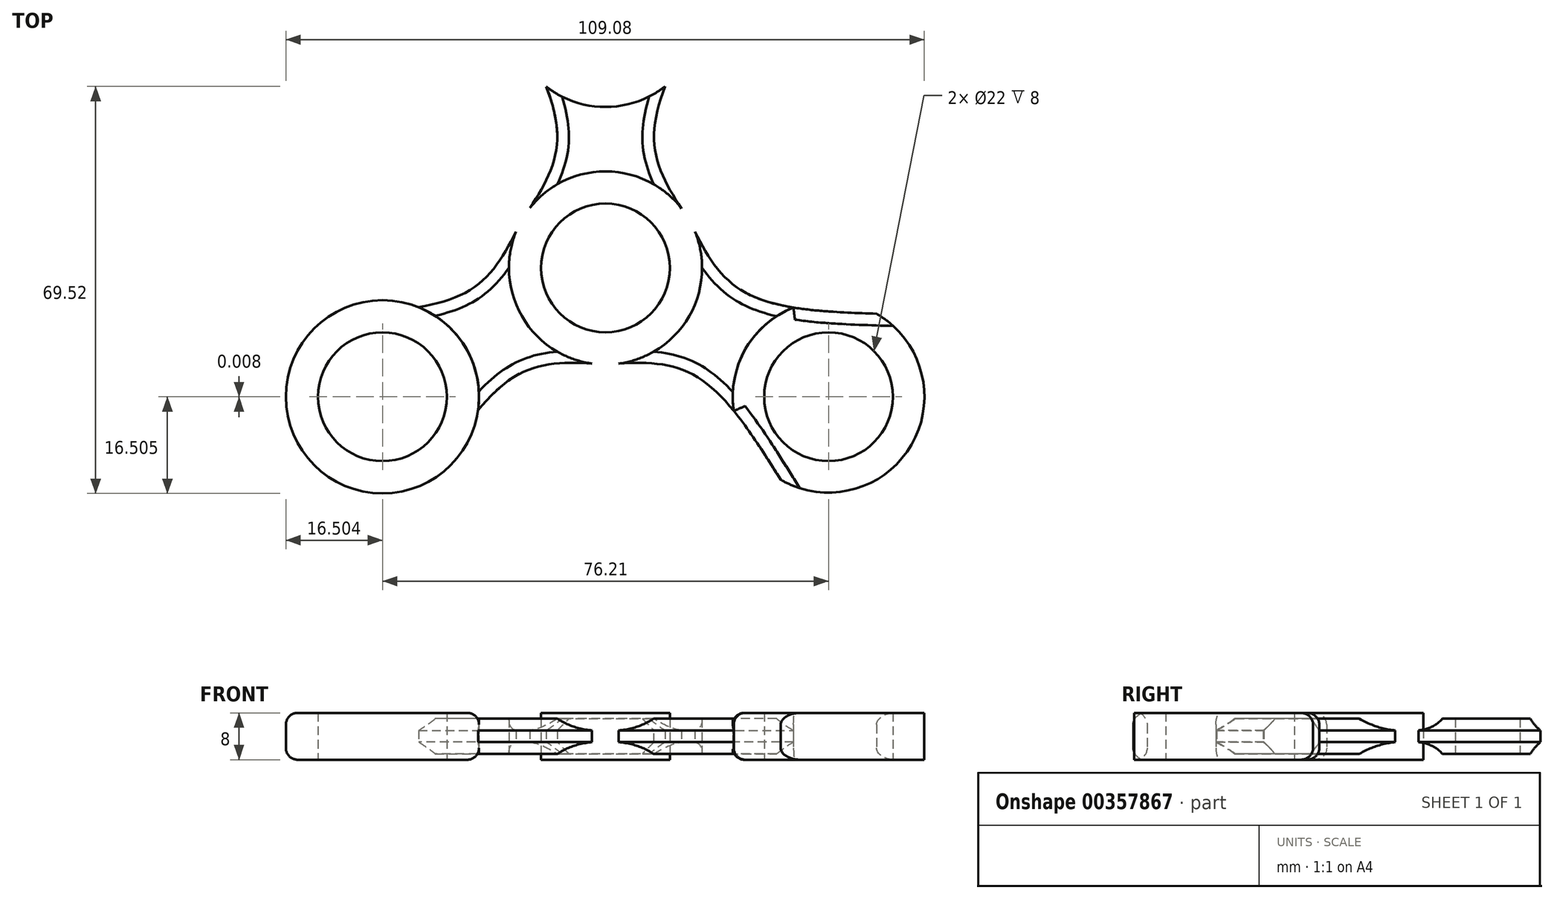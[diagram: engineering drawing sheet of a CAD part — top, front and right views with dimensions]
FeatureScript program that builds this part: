
annotation { "Feature Type Name" : "Feature", "Feature Type Description" : "" }
export const myFeature = defineFeature(function(context is Context, id is Id, definition is map)
    precondition{}
    {
        {
            var Q0;
            Q0=qCreatedBy(makeId("Top.planeOp"),FACE);
            var sketch = newSketch(context, id + "F0", { "sketchPlane" : qUnion([Q0])});
            skCircle(sketch, "E0", {"center": v(0.06, -10.15) * mm, "radius": 11 * mm});
            skCircle(sketch, "E1", {"center": v(0.06, 33.85) * mm, "radius": 11 * mm});
            skCircle(sketch, "E2", {"center": v(38.16, -32.15) * mm, "radius": 11 * mm});
            skCircle(sketch, "E3", {"center": v(-38.05, -32.16) * mm, "radius": 11 * mm});
            skCircle(sketch, "E4.0", {"center": v(0.06, -10.15) * mm, "radius": 16.5 * mm});
            skCircle(sketch, "E5.0", {"center": v(0.06, 33.85) * mm, "radius": 16.5 * mm});
            skCircle(sketch, "E6.0", {"center": v(-38.05, -32.16) * mm, "radius": 16.5 * mm});
            skLineSegment(sketch, "E7", {"start": v(0.06, 11.85) * mm, "end": v(0.06, 11.85) * mm});
            skPoint(sketch, "E8.endSnap0", {"position": v(19.11, -21.15) * mm});
            skLineSegment(sketch, "E9", {"start": v(29.98, -46.32) * mm, "end": v(29.98, -46.32) * mm});
            skLineSegment(sketch, "E10", {"start": v(-10.06, 20.82) * mm, "end": v(-10.06, 20.82) * mm});
            skLineSegment(sketch, "E11", {"start": v(10.23, 20.86) * mm, "end": v(10.23, 20.86) * mm});
            skFitSpline(sketch, "E12", {"points": [v(46.35, -17.97) * mm, v(23.26, -13.96) * mm, v(14.35, -1.9) * mm], "startDerivative": vector(-47.53, 1.69) * mm, "endDerivative": vector(-15.28, 31.57) * mm});
            skLineSegment(sketch, "E13", {"start": v(21.98, -34.58) * mm, "end": v(21.98, -34.58) * mm});
            skArc(sketch, "E14", {"start": v(23.99, -23.96) * mm, "mid": v(22.08, -29.1) * mm, "end": v(21.98, -34.58) * mm});
            skFitSpline(sketch, "E15", {"points": [v(-29.8, -46.44) * mm, v(-14.84, -28.33) * mm, v(0.06, -26.65) * mm], "startDerivative": vector(25.05, 40.57) * mm, "endDerivative": vector(35.03, -2.6) * mm});
            skFitSpline(sketch, "E16", {"points": [v(16.56, 33.85) * mm, v(8.36, 11.85) * mm, v(14.35, -1.9) * mm], "startDerivative": vector(-22.6, -41.98) * mm, "endDerivative": vector(19.75, -29.04) * mm});
            skFitSpline(sketch, "E17", {"points": [v(-16.44, 33.85) * mm, v(-8.2, 11.85) * mm, v(-14.23, -1.9) * mm], "startDerivative": vector(22.75, -41.99) * mm, "endDerivative": vector(-19.91, -29.03) * mm});
            skArc(sketch, "E18", {"start": v(21.98, -34.58) * mm, "mid": v(24.64, -41.37) * mm, "end": v(29.98, -46.32) * mm});
            skArc(sketch, "E19", {"start": v(29.98, -46.32) * mm, "mid": v(53.98, -27.9) * mm, "end": v(23.99, -23.96) * mm});
            skFitSpline(sketch, "E20", {"points": [v(-46.3, -17.87) * mm, v(-23.14, -13.96) * mm, v(-14.23, -1.9) * mm], "startDerivative": vector(47.65, 1.44) * mm, "endDerivative": vector(15.27, 31.62) * mm});
            skFitSpline(sketch, "E21", {"points": [v(0.06, -26.65) * mm, v(14.96, -28.33) * mm, v(29.98, -46.32) * mm], "startDerivative": vector(34.97, 2.55) * mm, "endDerivative": vector(25.23, -40.32) * mm});
            skSolve(sketch);
        }
        {
            var Q0;
            {var subQ0=sQuery(id+"F0.wireOp",EDGE,"E20");var subQ1=sQuery(id+"F0.wireOp",EDGE,"E4.0");var subQ2=makeQuery(id+"F0.imprint","INTERSECT",VERTEX,{"derivedFrom":[subQ1,subQ0]});Q0=makeQuery(id+"F0.imprint","IMPRINT",FACE,{"disambiguationData":[TD([[makeQuery(id+"F0.imprint","IMPRINT",EDGE,{"disambiguationData":[TD([[subQ2,-1.0]])],"derivedFrom":subQ1}),-1.0]])]});}
            var Q1;
            {var subQ0=sQuery(id+"F0.wireOp",EDGE,"E16");var subQ1=sQuery(id+"F0.wireOp",EDGE,"E4.0");var subQ2=makeQuery(id+"F0.imprint","INTERSECT",VERTEX,{"derivedFrom":[subQ1,subQ0]});Q1=makeQuery(id+"F0.imprint","IMPRINT",FACE,{"disambiguationData":[TD([[makeQuery(id+"F0.imprint","IMPRINT",EDGE,{"disambiguationData":[TD([[subQ2,-1.0]])],"derivedFrom":subQ1}),-1.0]])]});}
            var Q2;
            {var subQ3=sQuery(id+"F0.wireOp",EDGE,"E14");Q2=makeQuery(id+"F0.imprint","IMPRINT",FACE,{"disambiguationData":[TD([[makeQuery(id+"F0.imprint","IMPRINT",EDGE,{"derivedFrom":subQ3}),-1.0]])]});}
            extrude(context, id + "F1", {"entities" : qUnion([Q0, Q1, Q2]), "depth" : 6 * mm, "symmetric" : true});
        }
        {
            var Q0;
            Q0=makeQuery(id+"F0.imprint","IMPRINT",FACE,{"disambiguationData":[TD([[makeQuery(id+"F0.imprint","IMPRINT",EDGE,{"derivedFrom":sQuery(id+"F0.wireOp",EDGE,"E1")}),-1.0]])]});
            var Q1;
            Q1=makeQuery(id+"F0.imprint","IMPRINT",FACE,{"disambiguationData":[TD([[makeQuery(id+"F0.imprint","IMPRINT",EDGE,{"derivedFrom":sQuery(id+"F0.wireOp",EDGE,"E0")}),1.0]])]});
            var Q2;
            Q2=makeQuery(id+"F0.imprint","IMPRINT",FACE,{"disambiguationData":[TD([[makeQuery(id+"F0.imprint","IMPRINT",EDGE,{"derivedFrom":sQuery(id+"F0.wireOp",EDGE,"E2")}),-1.0]])]});
            var Q3;
            Q3=makeQuery(id+"F0.imprint","IMPRINT",FACE,{"disambiguationData":[TD([[makeQuery(id+"F0.imprint","IMPRINT",EDGE,{"derivedFrom":sQuery(id+"F0.wireOp",EDGE,"E3")}),-1.0]])]});
            extrude(context, id + "F2", {"entities" : qUnion([Q0, Q1, Q2, Q3]), "depth" : 8 * mm, "symmetric" : true});
        }
        {
            var Q0;
            Q0=makeQuery(id+"F2.opExtrude","CAP_EDGE",EDGE,{"disambiguationData":[OSD([sQuery(id+"F0.wireOp",EDGE,"E5.0")])],"isStart":false});
            var Q1;
            Q1=makeQuery(id+"F2.opExtrude","CAP_EDGE",EDGE,{"disambiguationData":[OSD([sQuery(id+"F0.wireOp",EDGE,"E14"),sQuery(id+"F0.wireOp",EDGE,"E18"),sQuery(id+"F0.wireOp",EDGE,"E19")])],"isStart":false});
            var Q2;
            Q2=makeQuery(id+"F2.opExtrude","CAP_EDGE",EDGE,{"disambiguationData":[OSD([sQuery(id+"F0.wireOp",EDGE,"E14"),sQuery(id+"F0.wireOp",EDGE,"E18"),sQuery(id+"F0.wireOp",EDGE,"E19")])],"isStart":true});
            var Q3;
            Q3=makeQuery(id+"F2.opExtrude","CAP_EDGE",EDGE,{"disambiguationData":[OSD([sQuery(id+"F0.wireOp",EDGE,"E5.0")])],"isStart":true});
            var Q4;
            Q4=makeQuery(id+"F2.opExtrude","CAP_EDGE",EDGE,{"disambiguationData":[OSD([sQuery(id+"F0.wireOp",EDGE,"E6.0")])],"isStart":false});
            var Q5;
            Q5=makeQuery(id+"F2.opExtrude","CAP_EDGE",EDGE,{"disambiguationData":[OSD([sQuery(id+"F0.wireOp",EDGE,"E6.0")])],"isStart":true});
            var Q6;
            {var subQ0=sQuery(id+"F0.wireOp",EDGE,"E4.0");Q6=makeQuery(id+"F2.opExtrude","CAP_EDGE",EDGE,{"disambiguationData":[OSD([subQ0]),TDD([makeQuery(id+"F0.imprint","IMPRINT",EDGE,{"disambiguationData":[TD([[makeQuery(id+"F0.imprint","INTERSECT",VERTEX,{"derivedFrom":[subQ0,sQuery(id+"F0.wireOp",EDGE,"E12")]}),1.0]])],"derivedFrom":subQ0})])],"isStart":false});}
            var Q7;
            {var subQ0=sQuery(id+"F0.wireOp",EDGE,"E4.0");Q7=makeQuery(id+"F2.opExtrude","CAP_EDGE",EDGE,{"disambiguationData":[OSD([subQ0]),TDD([makeQuery(id+"F0.imprint","IMPRINT",EDGE,{"disambiguationData":[TD([[makeQuery(id+"F0.imprint","INTERSECT",VERTEX,{"derivedFrom":[subQ0,sQuery(id+"F0.wireOp",EDGE,"E16")]}),-1.0]])],"derivedFrom":subQ0})])],"isStart":false});}
            var Q8;
            {var subQ0=sQuery(id+"F0.wireOp",EDGE,"E4.0");Q8=makeQuery(id+"F2.opExtrude","CAP_EDGE",EDGE,{"disambiguationData":[OSD([subQ0]),TDD([makeQuery(id+"F0.imprint","IMPRINT",EDGE,{"disambiguationData":[TD([[makeQuery(id+"F0.imprint","INTERSECT",VERTEX,{"derivedFrom":[subQ0,sQuery(id+"F0.wireOp",EDGE,"E20")]}),-1.0]])],"derivedFrom":subQ0})])],"isStart":false});}
            var Q9;
            Q9=makeQuery(id+"F2.opExtrude","CAP_EDGE",EDGE,{"disambiguationData":[OSD([sQuery(id+"F0.wireOp",EDGE,"E15")])],"isStart":false});
            var Q10;
            Q10=makeQuery(id+"F2.opExtrude","CAP_EDGE",EDGE,{"disambiguationData":[OSD([sQuery(id+"F0.wireOp",EDGE,"E21")])],"isStart":false});
            var Q11;
            Q11=makeQuery(id+"F2.opExtrude","CAP_EDGE",EDGE,{"disambiguationData":[OSD([sQuery(id+"F0.wireOp",EDGE,"E12")])],"isStart":false});
            var Q12;
            Q12=makeQuery(id+"F2.opExtrude","CAP_EDGE",EDGE,{"disambiguationData":[OSD([sQuery(id+"F0.wireOp",EDGE,"E16")])],"isStart":false});
            var Q13;
            Q13=makeQuery(id+"F2.opExtrude","CAP_EDGE",EDGE,{"disambiguationData":[OSD([sQuery(id+"F0.wireOp",EDGE,"E17")])],"isStart":false});
            var Q14;
            Q14=makeQuery(id+"F2.opExtrude","CAP_EDGE",EDGE,{"disambiguationData":[OSD([sQuery(id+"F0.wireOp",EDGE,"E20")])],"isStart":false});
            var Q15;
            {var subQ0=sQuery(id+"F0.wireOp",EDGE,"E4.0");Q15=makeQuery(id+"F2.opExtrude","CAP_EDGE",EDGE,{"disambiguationData":[OSD([subQ0]),TDD([makeQuery(id+"F0.imprint","IMPRINT",EDGE,{"disambiguationData":[TD([[makeQuery(id+"F0.imprint","INTERSECT",VERTEX,{"derivedFrom":[subQ0,sQuery(id+"F0.wireOp",EDGE,"E12")]}),1.0]])],"derivedFrom":subQ0})])],"isStart":true});}
            var Q16;
            Q16=makeQuery(id+"F2.opExtrude","CAP_EDGE",EDGE,{"disambiguationData":[OSD([sQuery(id+"F0.wireOp",EDGE,"E16")])],"isStart":true});
            var Q17;
            Q17=makeQuery(id+"F2.opExtrude","CAP_EDGE",EDGE,{"disambiguationData":[OSD([sQuery(id+"F0.wireOp",EDGE,"E12")])],"isStart":true});
            var Q18;
            Q18=makeQuery(id+"F2.opExtrude","CAP_EDGE",EDGE,{"disambiguationData":[OSD([sQuery(id+"F0.wireOp",EDGE,"E17")])],"isStart":true});
            var Q19;
            Q19=makeQuery(id+"F2.opExtrude","CAP_EDGE",EDGE,{"disambiguationData":[OSD([sQuery(id+"F0.wireOp",EDGE,"E20")])],"isStart":true});
            var Q20;
            {var subQ0=sQuery(id+"F0.wireOp",EDGE,"E4.0");Q20=makeQuery(id+"F2.opExtrude","CAP_EDGE",EDGE,{"disambiguationData":[OSD([subQ0]),TDD([makeQuery(id+"F0.imprint","IMPRINT",EDGE,{"disambiguationData":[TD([[makeQuery(id+"F0.imprint","INTERSECT",VERTEX,{"derivedFrom":[subQ0,sQuery(id+"F0.wireOp",EDGE,"E20")]}),-1.0]])],"derivedFrom":subQ0})])],"isStart":true});}
            var Q21;
            Q21=makeQuery(id+"F2.opExtrude","CAP_EDGE",EDGE,{"disambiguationData":[OSD([sQuery(id+"F0.wireOp",EDGE,"E21")])],"isStart":true});
            var Q22;
            Q22=makeQuery(id+"F2.opExtrude","CAP_EDGE",EDGE,{"disambiguationData":[OSD([sQuery(id+"F0.wireOp",EDGE,"E15")])],"isStart":true});
            var Q23;
            {var subQ0=sQuery(id+"F0.wireOp",EDGE,"E4.0");Q23=makeQuery(id+"F2.opExtrude","CAP_EDGE",EDGE,{"disambiguationData":[OSD([subQ0]),TDD([makeQuery(id+"F0.imprint","IMPRINT",EDGE,{"disambiguationData":[TD([[makeQuery(id+"F0.imprint","INTERSECT",VERTEX,{"derivedFrom":[subQ0,sQuery(id+"F0.wireOp",EDGE,"E16")]}),-1.0]])],"derivedFrom":subQ0})])],"isStart":true});}
            fillet(context, id + "F3", {"entities" : qUnion([Q0, Q1, Q2, Q3, Q4, Q5, Q6, Q7, Q8, Q9, Q10, Q11, Q12, Q13, Q14, Q15, Q16, Q17, Q18, Q19, Q20, Q21, Q22, Q23]), "radius" : 2 * mm, "tangentPropagation" : true, "allowEdgeOverflow" : false});
        }
        {
            var Q0;
            Q0=makeQuery(id+"F1.opExtrude","CAP_EDGE",EDGE,{"disambiguationData":[OSD([sQuery(id+"F0.wireOp",EDGE,"E17")])],"isStart":true});
            var Q1;
            Q1=makeQuery(id+"F1.opExtrude","CAP_EDGE",EDGE,{"disambiguationData":[OSD([sQuery(id+"F0.wireOp",EDGE,"E20")])],"isStart":true});
            var Q2;
            Q2=makeQuery(id+"F1.opExtrude","CAP_EDGE",EDGE,{"disambiguationData":[OSD([sQuery(id+"F0.wireOp",EDGE,"E15")])],"isStart":true});
            var Q3;
            Q3=makeQuery(id+"F1.opExtrude","CAP_EDGE",EDGE,{"disambiguationData":[OSD([sQuery(id+"F0.wireOp",EDGE,"E21")])],"isStart":true});
            var Q4;
            Q4=makeQuery(id+"F1.opExtrude","CAP_EDGE",EDGE,{"disambiguationData":[OSD([sQuery(id+"F0.wireOp",EDGE,"E12")])],"isStart":true});
            var Q5;
            Q5=makeQuery(id+"F1.opExtrude","CAP_EDGE",EDGE,{"disambiguationData":[OSD([sQuery(id+"F0.wireOp",EDGE,"E16")])],"isStart":true});
            var Q6;
            Q6=makeQuery(id+"F1.opExtrude","CAP_EDGE",EDGE,{"disambiguationData":[OSD([sQuery(id+"F0.wireOp",EDGE,"E17")])],"isStart":false});
            var Q7;
            Q7=makeQuery(id+"F1.opExtrude","CAP_EDGE",EDGE,{"disambiguationData":[OSD([sQuery(id+"F0.wireOp",EDGE,"E15")])],"isStart":false});
            var Q8;
            Q8=makeQuery(id+"F1.opExtrude","CAP_EDGE",EDGE,{"disambiguationData":[OSD([sQuery(id+"F0.wireOp",EDGE,"E20")])],"isStart":false});
            var Q9;
            Q9=makeQuery(id+"F1.opExtrude","CAP_EDGE",EDGE,{"disambiguationData":[OSD([sQuery(id+"F0.wireOp",EDGE,"E21")])],"isStart":false});
            var Q10;
            Q10=makeQuery(id+"F1.opExtrude","CAP_EDGE",EDGE,{"disambiguationData":[OSD([sQuery(id+"F0.wireOp",EDGE,"E12")])],"isStart":false});
            var Q11;
            Q11=makeQuery(id+"F1.opExtrude","CAP_EDGE",EDGE,{"disambiguationData":[OSD([sQuery(id+"F0.wireOp",EDGE,"E16")])],"isStart":false});
            chamfer(context, id + "F4", {"entities" : qUnion([Q0, Q1, Q2, Q3, Q4, Q5, Q6, Q7, Q8, Q9, Q10, Q11]), "width" : 2 * mm, "tangentPropagation" : true});
        }
    });
